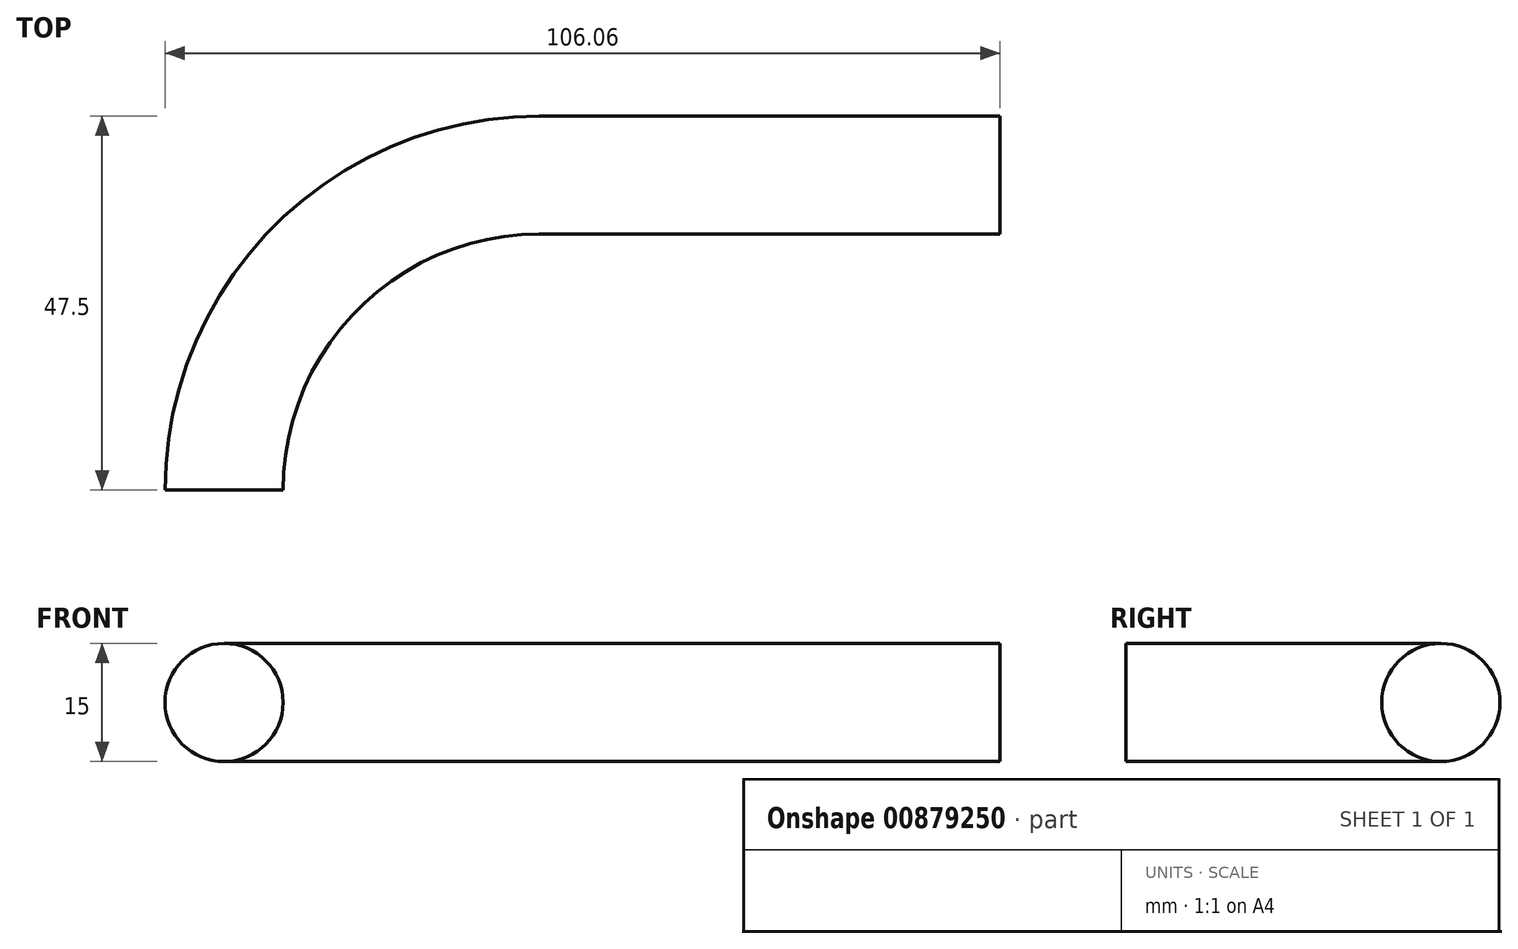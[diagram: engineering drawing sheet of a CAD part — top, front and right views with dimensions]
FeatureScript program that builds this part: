
annotation { "Feature Type Name" : "Feature", "Feature Type Description" : "" }
export const myFeature = defineFeature(function(context is Context, id is Id, definition is map)
    precondition{}
    {
        {
            var Q0;
            Q0=qCreatedBy(makeId("Top.planeOp"),FACE);
            var sketch = newSketch(context, id + "F0", { "sketchPlane" : qUnion([Q0])});
            skLineSegment(sketch, "E0", {"start": v(0, 40) * mm, "end": v(-58.56, 40) * mm});
            skArc(sketch, "E1", {"start": v(-58.56, 40) * mm, "mid": v(-86.85, 28.28) * mm, "end": v(-98.56, 0) * mm});
            skSolve(sketch);
        }
        {
            var Q0;
            Q0=qCreatedBy(makeId("Front.planeOp"),FACE);
            var sketch = newSketch(context, id + "F1", { "sketchPlane" : qUnion([Q0])});
            skCircle(sketch, "E2", {"center": v(-98.56, 0) * mm, "radius": 7.5 * mm});
            skSolve(sketch);
        }
        {
            var Q0;
            Q0=makeQuery(id+"F1.imprint","IMPRINT",FACE,{"disambiguationData":[TD([[makeQuery(id+"F1.imprint","IMPRINT",EDGE,{"derivedFrom":sQuery(id+"F1.wireOp",EDGE,"E2")}),1.0]])]});
            var Q1;
            Q1=sQuery(id+"F0.wireOp",EDGE,"E0");
            var Q2;
            Q2=sQuery(id+"F0.wireOp",EDGE,"E1");
            sweep(context, id + "F2", {"profiles" : qUnion([Q0]), "path" : qUnion([Q1, Q2])});
        }
    });
